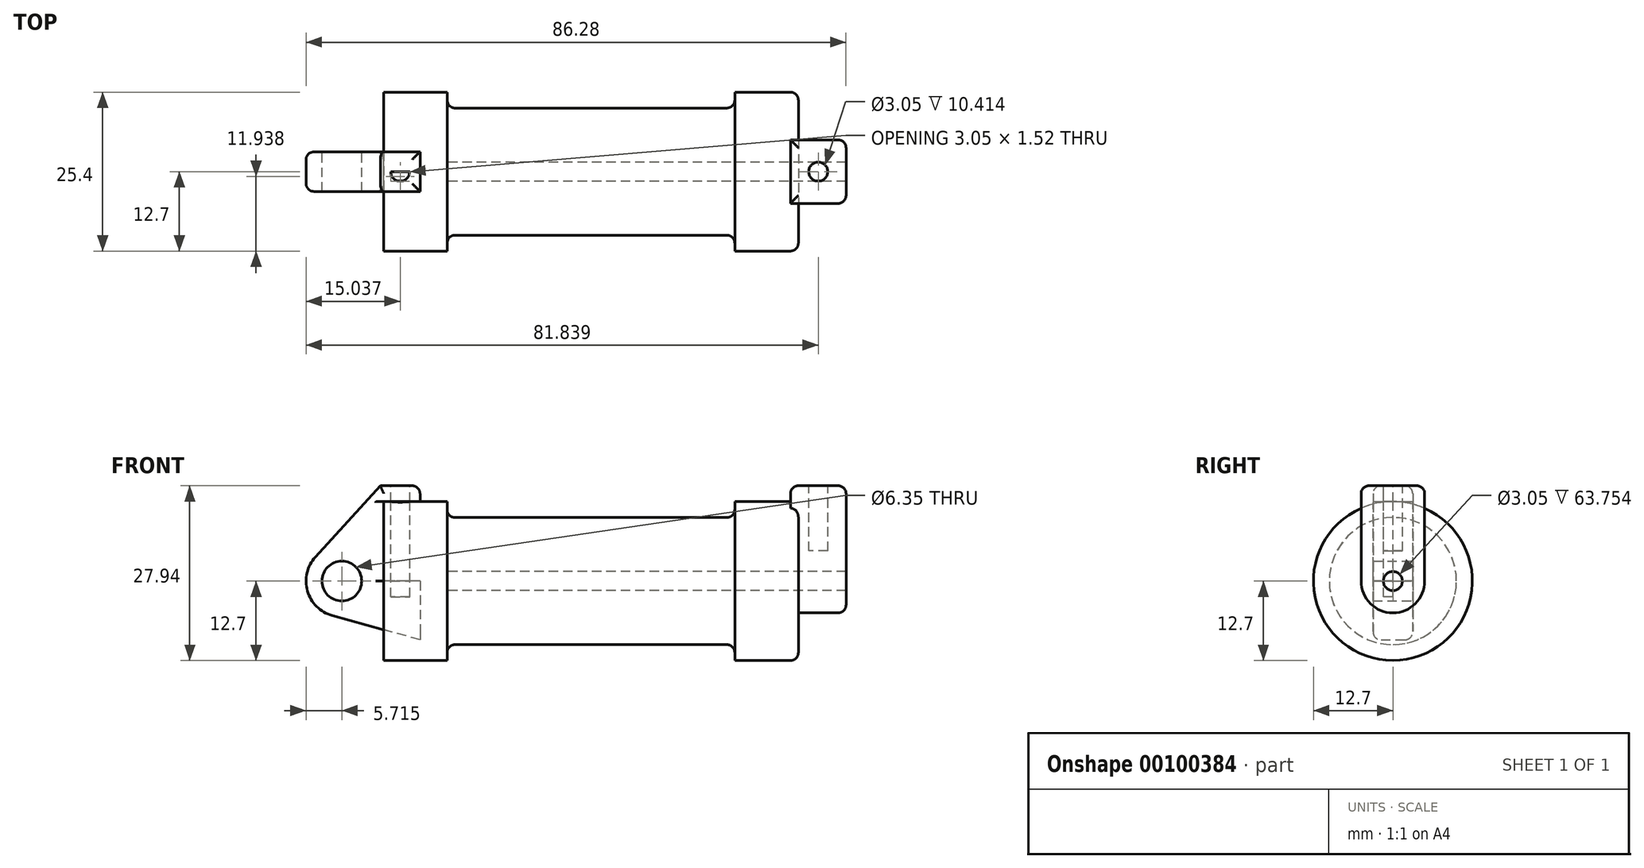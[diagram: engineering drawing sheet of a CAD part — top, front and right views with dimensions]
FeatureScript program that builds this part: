
annotation { "Feature Type Name" : "Feature", "Feature Type Description" : "" }
export const myFeature = defineFeature(function(context is Context, id is Id, definition is map)
    precondition{}
    {
        {
            var Q0;
            Q0=qCreatedBy(makeId("Front.planeOp"),FACE);
            var sketch = newSketch(context, id + "F0", { "sketchPlane" : qUnion([Q0])});
            skLineSegment(sketch, "E0", {"start": v(0, 0) * mm, "end": v(0, 12.7) * mm});
            skLineSegment(sketch, "E1", {"start": v(0, 12.7) * mm, "end": v(10.16, 12.7) * mm});
            skLineSegment(sketch, "E2", {"start": v(10.16, 12.7) * mm, "end": v(10.16, 10.16) * mm});
            skLineSegment(sketch, "E3", {"start": v(10.16, 10.16) * mm, "end": v(56.13, 10.16) * mm});
            skLineSegment(sketch, "E4", {"start": v(56.13, 10.16) * mm, "end": v(56.13, 12.7) * mm});
            skLineSegment(sketch, "E5", {"start": v(56.13, 12.7) * mm, "end": v(66.3, 12.7) * mm});
            skLineSegment(sketch, "E6", {"start": v(66.3, 12.7) * mm, "end": v(66.3, 0) * mm});
            skLineSegment(sketch, "E7", {"start": v(66.3, 0) * mm, "end": v(0, 0) * mm});
            skLineSegment(sketch, "E8", {"start": v(5.84, 15.24) * mm, "end": v(-0.5, 15.24) * mm});
            skLineSegment(sketch, "E9", {"start": v(-0.5, 15.24) * mm, "end": v(-10.88, 3.85) * mm});
            skLineSegment(sketch, "E10", {"start": v(0, 0) * mm, "end": v(-6.65, 0) * mm});
            skCircle(sketch, "E11", {"center": v(-6.65, 0) * mm, "radius": 5.72 * mm});
            skCircle(sketch, "E12", {"center": v(-6.65, 0) * mm, "radius": 3.18 * mm});
            skLineSegment(sketch, "E13", {"start": v(5.84, 15.24) * mm, "end": v(5.84, -9.4) * mm});
            skLineSegment(sketch, "E14", {"start": v(5.84, -9.4) * mm, "end": v(-8.18, -5.5) * mm});
            skText(sketch, "E15", { "text": "The volume of the part is 1.676 in3.", "fontName": "OpenSans-Regular.ttf"});
            const initialGuessF0  = {"E15": [0.19486, -0.04244, 1, 0, 0.03059]};
            skSetInitialGuess(sketch, initialGuessF0);
            skSolve(sketch);
        }
        {
            var Q0;
            {var subQ0=sQuery(id+"F0.wireOp",EDGE,"E2");Q0=makeQuery(id+"F0.imprint","IMPRINT",FACE,{"disambiguationData":[TD([[makeQuery(id+"F0.imprint","IMPRINT",EDGE,{"derivedFrom":subQ0}),-1.0]])]});}
            var Q1;
            {var subQ0=sQuery(id+"F0.wireOp",EDGE,"E0");Q1=makeQuery(id+"F0.imprint","IMPRINT",FACE,{"disambiguationData":[TD([[makeQuery(id+"F0.imprint","IMPRINT",EDGE,{"derivedFrom":subQ0}),-1.0]])]});}
            var Q2;
            Q2 = qSketchRegion(id + "F4", true);
            var Q3;
            Q3=sQuery(id+"F0.wireOp",EDGE,"E7");
            revolve(context, id + "F1", {"entities" : qUnion([Q0, Q1, Q2]), "axis" : qUnion([Q3]), "revolveType" : RevolveType.FULL});
        }
        {
            var Q0;
            {var subQ3=sQuery(id+"F0.wireOp",EDGE,"E0");Q0=makeQuery(id+"F0.imprint","IMPRINT",FACE,{"disambiguationData":[TD([[makeQuery(id+"F0.imprint","IMPRINT",EDGE,{"derivedFrom":subQ3}),1.0]])]});}
            var Q1;
            {var subQ4=sQuery(id+"F0.wireOp",EDGE,"E12");Q1=makeQuery(id+"F0.imprint","IMPRINT",FACE,{"disambiguationData":[TD([[makeQuery(id+"F0.imprint","IMPRINT",EDGE,{"derivedFrom":subQ4}),-1.0]])]});}
            var Q2;
            {var subQ0=sQuery(id+"F0.wireOp",EDGE,"E14");Q2=makeQuery(id+"F0.imprint","IMPRINT",FACE,{"disambiguationData":[TD([[makeQuery(id+"F0.imprint","IMPRINT",EDGE,{"derivedFrom":subQ0}),-1.0]])]});}
            extrude(context, id + "F2", {"entities" : qUnion([Q0, Q1, Q2]), "oppositeDirection" : true, "depth" : 3.17 * mm});
        }
        {
            var Q0;
            {var subQ3=sQuery(id+"F0.wireOp",EDGE,"E0");Q0=makeQuery(id+"F0.imprint","IMPRINT",FACE,{"disambiguationData":[TD([[makeQuery(id+"F0.imprint","IMPRINT",EDGE,{"derivedFrom":subQ3}),1.0]])]});}
            var Q1;
            {var subQ0=sQuery(id+"F0.wireOp",EDGE,"E14");Q1=makeQuery(id+"F0.imprint","IMPRINT",FACE,{"disambiguationData":[TD([[makeQuery(id+"F0.imprint","IMPRINT",EDGE,{"derivedFrom":subQ0}),-1.0]])]});}
            var Q2;
            {var subQ4=sQuery(id+"F0.wireOp",EDGE,"E12");Q2=makeQuery(id+"F0.imprint","IMPRINT",FACE,{"disambiguationData":[TD([[makeQuery(id+"F0.imprint","IMPRINT",EDGE,{"derivedFrom":subQ4}),-1.0]])]});}
            extrude(context, id + "F3", {"entities" : qUnion([Q0, Q1, Q2]), "depth" : 3.17 * mm});
        }
        {
            var Q0;
            Q0=makeQuery(id+"F2.opExtrude","SWEPT_FACE",FACE,{"disambiguationData":[OSD([sQuery(id+"F0.wireOp",EDGE,"E8")])]});
            var sketch = newSketch(context, id + "F4", { "sketchPlane" : qUnion([Q0])});
            skSolve(sketch);
        }
        {
            var Q0;
            Q0=makeQuery(id+"F3.opExtrude","SWEPT_FACE",FACE,{"disambiguationData":[OSD([sQuery(id+"F0.wireOp",EDGE,"E8")])]});
            var sketch = newSketch(context, id + "F5", { "sketchPlane" : qUnion([Q0])});
            skCircle(sketch, "E16", {"center": v(2.67, 0) * mm, "radius": 1.52 * mm});
            skSolve(sketch);
        }
        {
            var Q0;
            Q0=makeQuery(id+"F2.opExtrude","SWEPT_BODY",BODY,{"disambiguationData":[OSD([sQuery(id+"F0.wireOp",EDGE,"E0"),sQuery(id+"F0.wireOp",EDGE,"E1"),sQuery(id+"F0.wireOp",EDGE,"E7"),sQuery(id+"F0.wireOp",EDGE,"E8"),sQuery(id+"F0.wireOp",EDGE,"E9"),sQuery(id+"F0.wireOp",EDGE,"E11"),sQuery(id+"F0.wireOp",EDGE,"E12"),sQuery(id+"F0.wireOp",EDGE,"E13"),sQuery(id+"F0.wireOp",EDGE,"E14")])]});
            var Q1;
            Q1=makeQuery(id+"F3.opExtrude","SWEPT_BODY",BODY,{"disambiguationData":[OSD([sQuery(id+"F0.wireOp",EDGE,"E0"),sQuery(id+"F0.wireOp",EDGE,"E1"),sQuery(id+"F0.wireOp",EDGE,"E7"),sQuery(id+"F0.wireOp",EDGE,"E8"),sQuery(id+"F0.wireOp",EDGE,"E9"),sQuery(id+"F0.wireOp",EDGE,"E11"),sQuery(id+"F0.wireOp",EDGE,"E12"),sQuery(id+"F0.wireOp",EDGE,"E13"),sQuery(id+"F0.wireOp",EDGE,"E14")])]});
            deleteBodies(context, id + "F6", {"entities" : qUnion([Q0, Q1])});
        }
        {
            var Q0;
            Q0=makeQuery(id+"F1.opRevolve","SWEPT_FACE",FACE,{"disambiguationData":[OSD([sQuery(id+"F0.wireOp",EDGE,"E6")])]});
            var sketch = newSketch(context, id + "F7", { "sketchPlane" : qUnion([Q0])});
            skCircle(sketch, "E17", {"center": v(0, 0) * mm, "radius": 1.52 * mm});
            skCircle(sketch, "E18", {"center": v(0, 0) * mm, "radius": 5.08 * mm});
            skLineSegment(sketch, "E19", {"start": v(5.08, 0) * mm, "end": v(5.08, 15.24) * mm});
            skLineSegment(sketch, "E20", {"start": v(-5.08, 0) * mm, "end": v(-5.08, 15.24) * mm});
            skLineSegment(sketch, "E21", {"start": v(-5.08, 15.24) * mm, "end": v(5.08, 15.24) * mm});
            skSolve(sketch);
        }
        {
            var Q0;
            Q0=makeQuery(id+"F7.imprint","IMPRINT",FACE,{"disambiguationData":[TD([[makeQuery(id+"F7.imprint","IMPRINT",EDGE,{"derivedFrom":sQuery(id+"F7.wireOp",EDGE,"E17")}),-1.0]])]});
            var Q1;
            {var subQ0=sQuery(id+"F7.wireOp",EDGE,"E19");var subQ1=sQuery(id+"F7.wireOp",EDGE,"E18");var subQ2=makeQuery(id+"F7.imprint","INTERSECT",VERTEX,{"derivedFrom":[subQ1,subQ0]});Q1=makeQuery(id+"F7.imprint","IMPRINT",FACE,{"disambiguationData":[TD([[makeQuery(id+"F7.imprint","IMPRINT",EDGE,{"disambiguationData":[TD([[subQ2,-1.0]])],"derivedFrom":subQ1}),-1.0]])]});}
            var Q2;
            {var subQ0=sQuery(id+"F7.wireOp",EDGE,"E21");Q2=makeQuery(id+"F7.imprint","IMPRINT",FACE,{"disambiguationData":[TD([[makeQuery(id+"F7.imprint","IMPRINT",EDGE,{"derivedFrom":subQ0}),-1.0]])]});}
            extrude(context, id + "F8", {"entities" : qUnion([Q0, Q1, Q2]), "operationType" : NewBodyOperationType.ADD, "depth" : 7.62 * mm});
        }
        {
            var Q0;
            Q0=makeQuery(id+"F8.opExtrude","CAP_FACE",FACE,{"disambiguationData":[OSD([sQuery(id+"F7.wireOp",EDGE,"E17"),sQuery(id+"F7.wireOp",EDGE,"E18"),sQuery(id+"F7.wireOp",EDGE,"E19"),sQuery(id+"F7.wireOp",EDGE,"E20"),sQuery(id+"F7.wireOp",EDGE,"E21")])],"isStart":true});
            extrude(context, id + "F9", {"entities" : qUnion([Q0]), "operationType" : NewBodyOperationType.ADD, "depth" : 1.27 * mm});
        }
        {
            var Q0;
            Q0=makeQuery(id+"F8.boolean.opBoolean","SPLIT",FACE,{"disambiguationData":[TD([makeQuery(id+"F8.opExtrude","SWEPT_FACE",FACE,{"disambiguationData":[OSD([sQuery(id+"F7.wireOp",EDGE,"E17")])]})])],"derivedFrom":makeQuery(id+"F1.opRevolve","SWEPT_FACE",FACE,{"disambiguationData":[OSD([sQuery(id+"F0.wireOp",EDGE,"E6")])]})});
            var Q1;
            Q1=makeQuery(id+"F1.opRevolve","SWEPT_FACE",FACE,{"disambiguationData":[OSD([sQuery(id+"F0.wireOp",EDGE,"E2")])]});
            extrude(context, id + "F10", {"entities" : qUnion([Q0]), "operationType" : NewBodyOperationType.REMOVE, "endBound" : BoundingType.UP_TO_SURFACE, "oppositeDirection" : true, "endBoundEntityFace" : qUnion([Q1]), "depth" : 25.4 * mm});
        }
        {
            var Q0;
            {var subQ0=sQuery(id+"F7.wireOp",EDGE,"E21");Q0=makeQuery(id+"F9.boolean.opBoolean","MERGE",FACE,{"derivedFrom":[makeQuery(id+"F8.opExtrude","SWEPT_FACE",FACE,{"disambiguationData":[OSD([subQ0])]}),makeQuery(id+"F9.opExtrude","SWEPT_FACE",FACE,{"disambiguationData":[OSD([subQ0])]})]});}
            var sketch = newSketch(context, id + "F11", { "sketchPlane" : qUnion([Q0])});
            skCircle(sketch, "E22", {"center": v(69.47, 0) * mm, "radius": 1.52 * mm});
            skSolve(sketch);
        }
        {
            var Q0;
            Q0=makeQuery(id+"F11.imprint","IMPRINT",FACE,{"disambiguationData":[TD([[makeQuery(id+"F11.imprint","IMPRINT",EDGE,{"derivedFrom":sQuery(id+"F11.wireOp",EDGE,"E22")}),1.0]])]});
            extrude(context, id + "F12", {"entities" : qUnion([Q0]), "operationType" : NewBodyOperationType.REMOVE, "oppositeDirection" : true, "depth" : 10.4 * mm});
        }
        {
            var Q0;
            {var subQ4=sQuery(id+"F0.wireOp",EDGE,"E12");Q0=makeQuery(id+"F0.imprint","IMPRINT",FACE,{"disambiguationData":[TD([[makeQuery(id+"F0.imprint","IMPRINT",EDGE,{"derivedFrom":subQ4}),-1.0]])]});}
            var Q1;
            {var subQ0=sQuery(id+"F0.wireOp",EDGE,"E14");Q1=makeQuery(id+"F0.imprint","IMPRINT",FACE,{"disambiguationData":[TD([[makeQuery(id+"F0.imprint","IMPRINT",EDGE,{"derivedFrom":subQ0}),-1.0]])]});}
            var Q2;
            {var subQ3=sQuery(id+"F0.wireOp",EDGE,"E0");Q2=makeQuery(id+"F0.imprint","IMPRINT",FACE,{"disambiguationData":[TD([[makeQuery(id+"F0.imprint","IMPRINT",EDGE,{"derivedFrom":subQ3}),1.0]])]});}
            extrude(context, id + "F13", {"entities" : qUnion([Q0, Q1, Q2]), "endBound" : BoundingType.SYMMETRIC, "depth" : 6.35 * mm});
        }
        {
            var Q0;
            {var subQ0=sQuery(id+"F0.wireOp",EDGE,"E8");Q0=makeQuery(id+"F4.imprint","IMPRINT",FACE,{"disambiguationData":[TD([[makeQuery(id+"F4.imprint","IMPRINT",EDGE,{"derivedFrom":makeQuery(id+"F2.opExtrude","CAP_EDGE",EDGE,{"disambiguationData":[OSD([subQ0])],"isStart":true})}),-1.0]])]});}
            var sketch = newSketch(context, id + "F14", { "sketchPlane" : qUnion([Q0])});
            skCircle(sketch, "E23", {"center": v(2.63, 0.1) * mm, "radius": 1.52 * mm});
            skSolve(sketch);
        }
        {
            var Q0;
            Q0 = qSketchRegion(id + "F14", true);
            var Q1;
            {var subQ0=sQuery(id+"F5.wireOp",EDGE,"E16");var subQ1=makeQuery(id+"F3.opExtrude","CAP_EDGE",EDGE,{"disambiguationData":[OSD([sQuery(id+"F0.wireOp",EDGE,"E8")])],"isStart":true});var subQ2=makeQuery(id+"F5.imprint","INTERSECT",VERTEX,{"disambiguationData":[OD(0.0)],"derivedFrom":[subQ1,subQ0]});Q1=makeQuery(id+"F5.imprint","IMPRINT",FACE,{"disambiguationData":[TD([[makeQuery(id+"F5.imprint","IMPRINT",EDGE,{"disambiguationData":[TD([[subQ2,1.0]])],"derivedFrom":subQ0}),1.0]])]});}
            extrude(context, id + "F15", {"entities" : qUnion([Q0, Q1]), "operationType" : NewBodyOperationType.REMOVE, "oppositeDirection" : true, "depth" : 17.78 * mm});
        }
        {
            var Q0;
            Q0=makeQuery(id+"F1.opRevolve","SWEPT_FACE",FACE,{"disambiguationData":[OSD([sQuery(id+"F0.wireOp",EDGE,"E3")])]});
            fillet(context, id + "F16", {"entities" : qUnion([Q0]), "radius" : 1.27 * mm, "tangentPropagation" : true, "allowEdgeOverflow" : false});
        }
        {
            var Q0;
            Q0=makeQuery(id+"F8.opExtrude","CAP_EDGE",EDGE,{"disambiguationData":[OSD([sQuery(id+"F7.wireOp",EDGE,"E18")])],"isStart":false});
            var Q1;
            Q1=makeQuery(id+"F8.boolean.opBoolean","SPLIT",EDGE,{"disambiguationData":[OD(1.0)],"derivedFrom":makeQuery(id+"F1.opRevolve","SWEPT_EDGE",EDGE,{"disambiguationData":[OSD([sQuery(id+"F0.wireOp",EDGE,"E5"),sQuery(id+"F0.wireOp",EDGE,"E6")])]})});
            var Q2;
            {var subQ0=sQuery(id+"F7.wireOp",EDGE,"E21");var subQ1=sQuery(id+"F7.wireOp",EDGE,"E19");Q2=makeQuery(id+"F9.boolean.opBoolean","MERGE",EDGE,{"derivedFrom":[makeQuery(id+"F8.opExtrude","SWEPT_EDGE",EDGE,{"disambiguationData":[OSD([subQ1,subQ0])]}),makeQuery(id+"F9.opExtrude","SWEPT_EDGE",EDGE,{"disambiguationData":[OSD([subQ1,subQ0])]})]});}
            var Q3;
            {var subQ0=sQuery(id+"F7.wireOp",EDGE,"E21");var subQ1=sQuery(id+"F7.wireOp",EDGE,"E20");Q3=makeQuery(id+"F9.boolean.opBoolean","MERGE",EDGE,{"derivedFrom":[makeQuery(id+"F8.opExtrude","SWEPT_EDGE",EDGE,{"disambiguationData":[OSD([subQ1,subQ0])]}),makeQuery(id+"F9.opExtrude","SWEPT_EDGE",EDGE,{"disambiguationData":[OSD([subQ1,subQ0])]})]});}
            var Q4;
            Q4=makeQuery(id+"F8.opExtrude","CAP_EDGE",EDGE,{"disambiguationData":[OSD([sQuery(id+"F7.wireOp",EDGE,"E21")])],"isStart":false});
            var Q5;
            Q5=makeQuery(id+"F9.opExtrude","CAP_EDGE",EDGE,{"disambiguationData":[OSD([sQuery(id+"F7.wireOp",EDGE,"E21")])],"isStart":false});
            var Q6;
            Q6=makeQuery(id+"F13.opExtrude","CAP_EDGE",EDGE,{"disambiguationData":[OSD([sQuery(id+"F0.wireOp",EDGE,"E11")])],"isStart":true});
            var Q7;
            Q7=makeQuery(id+"F13.opExtrude","CAP_EDGE",EDGE,{"disambiguationData":[OSD([sQuery(id+"F0.wireOp",EDGE,"E9")])],"isStart":false});
            var Q8;
            Q8=makeQuery(id+"F13.opExtrude","CAP_EDGE",EDGE,{"disambiguationData":[OSD([sQuery(id+"F0.wireOp",EDGE,"E14")])],"isStart":true});
            var Q9;
            Q9=makeQuery(id+"F13.opExtrude","CAP_EDGE",EDGE,{"disambiguationData":[OSD([sQuery(id+"F0.wireOp",EDGE,"E14")])],"isStart":false});
            var Q10;
            Q10=makeQuery(id+"F13.opExtrude","CAP_EDGE",EDGE,{"disambiguationData":[OSD([sQuery(id+"F0.wireOp",EDGE,"E8")])],"isStart":false});
            var Q11;
            Q11=makeQuery(id+"F13.opExtrude","SWEPT_EDGE",EDGE,{"disambiguationData":[OSD([sQuery(id+"F0.wireOp",EDGE,"E8"),sQuery(id+"F0.wireOp",EDGE,"E13")])]});
            var Q12;
            Q12=makeQuery(id+"F13.opExtrude","CAP_EDGE",EDGE,{"disambiguationData":[OSD([sQuery(id+"F0.wireOp",EDGE,"E8")])],"isStart":true});
            var Q13;
            Q13=makeQuery(id+"F13.opExtrude","CAP_EDGE",EDGE,{"disambiguationData":[OSD([sQuery(id+"F0.wireOp",EDGE,"E0")])],"isStart":false});
            var Q14;
            Q14=makeQuery(id+"F13.opExtrude","CAP_EDGE",EDGE,{"disambiguationData":[OSD([sQuery(id+"F0.wireOp",EDGE,"E9")])],"isStart":true});
            var Q15;
            Q15=makeQuery(id+"F13.opExtrude","CAP_EDGE",EDGE,{"disambiguationData":[OSD([sQuery(id+"F0.wireOp",EDGE,"E0")])],"isStart":true});
            fillet(context, id + "F17", {"entities" : qUnion([Q0, Q1, Q2, Q3, Q4, Q5, Q6, Q7, Q8, Q9, Q10, Q11, Q12, Q13, Q14, Q15]), "radius" : 1.27 * mm, "tangentPropagation" : true, "allowEdgeOverflow" : false});
        }
    });
